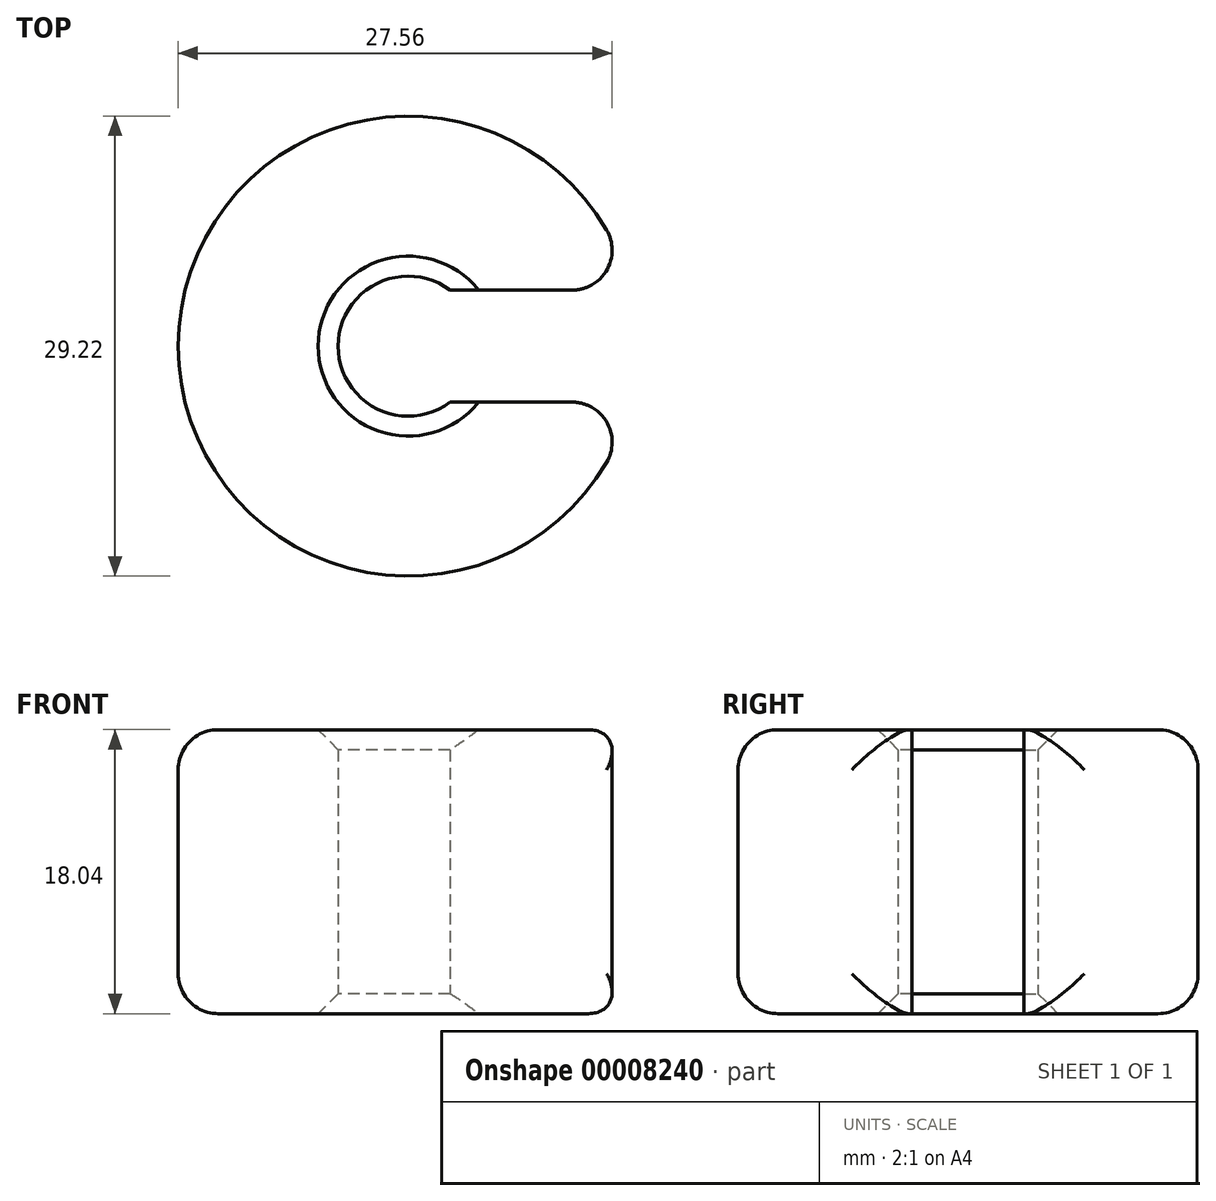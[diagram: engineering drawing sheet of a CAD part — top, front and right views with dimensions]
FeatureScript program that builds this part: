
annotation { "Feature Type Name" : "Feature", "Feature Type Description" : "" }
export const myFeature = defineFeature(function(context is Context, id is Id, definition is map)
    precondition{}
    {
        {
            var Q0;
            Q0=qCreatedBy(makeId("Top.planeOp"),FACE);
            var sketch = newSketch(context, id + "F0", { "sketchPlane" : qUnion([Q0])});
            skCircle(sketch, "E0", {"center": v(0, 0) * mm, "radius": 14.6 * mm});
            skCircle(sketch, "E1", {"center": v(0, 0) * mm, "radius": 4.45 * mm});
            skSolve(sketch);
        }
        {
            var Q0;
            Q0 = qSketchRegion(id + "F0", true);
            extrude(context, id + "F1", {"entities" : qUnion([Q0]), "endBound" : BoundingType.SYMMETRIC, "depth" : 18.03 * mm});
        }
        {
            var Q0;
            Q0=qCreatedBy(makeId("Top.planeOp"),FACE);
            var sketch = newSketch(context, id + "F2", { "sketchPlane" : qUnion([Q0])});
            skLineSegment(sketch, "E2.bottom", {"start": v(23.98, -3.56) * mm, "end": v(0, -3.56) * mm});
            skLineSegment(sketch, "E2.top", {"start": v(23.98, 3.56) * mm, "end": v(0, 3.56) * mm});
            skLineSegment(sketch, "E2.left", {"start": v(23.98, -3.56) * mm, "end": v(23.98, 3.56) * mm});
            skLineSegment(sketch, "E2.right", {"start": v(0, -3.56) * mm, "end": v(0, 3.56) * mm});
            skSolve(sketch);
        }
        {
            var Q0;
            Q0 = qSketchRegion(id + "F2", true);
            var Q1;
            Q1=makeQuery(id+"F1.opExtrude","CAP_FACE",FACE,{"disambiguationData":[OSD([sQuery(id+"F0.wireOp",EDGE,"E0"),sQuery(id+"F0.wireOp",EDGE,"E1")])],"isStart":true});
            extrude(context, id + "F3", {"entities" : qUnion([Q0]), "operationType" : NewBodyOperationType.REMOVE, "endBound" : BoundingType.UP_TO_SURFACE, "oppositeDirection" : true, "endBoundEntityFace" : qUnion([Q1]), "depth" : 25.4 * mm, "hasSecondDirection" : true, "secondDirectionOppositeDirection" : false, "secondDirectionDepth" : 25.4 * mm});
        }
        {
            var Q0;
            Q0=makeQuery(id+"F3.boolean.opBoolean","INTERSECT",EDGE,{"derivedFrom":[makeQuery(id+"F1.opExtrude","SWEPT_FACE",FACE,{"disambiguationData":[OSD([sQuery(id+"F0.wireOp",EDGE,"E0")])]}),makeQuery(id+"F3.opExtrude","SWEPT_FACE",FACE,{"disambiguationData":[OSD([sQuery(id+"F2.wireOp",EDGE,"E2.top")])]})]});
            var Q1;
            Q1=makeQuery(id+"F3.boolean.opBoolean","INTERSECT",EDGE,{"derivedFrom":[makeQuery(id+"F1.opExtrude","SWEPT_FACE",FACE,{"disambiguationData":[OSD([sQuery(id+"F0.wireOp",EDGE,"E0")])]}),makeQuery(id+"F3.opExtrude","SWEPT_FACE",FACE,{"disambiguationData":[OSD([sQuery(id+"F2.wireOp",EDGE,"E2.bottom")])]})]});
            fillet(context, id + "F4", {"entities" : qUnion([Q0, Q1]), "radius" : 2.54 * mm, "tangentPropagation" : true, "allowEdgeOverflow" : false});
        }
        {
            var Q0;
            Q0=makeQuery(id+"F1.opExtrude","SWEPT_FACE",FACE,{"disambiguationData":[OSD([sQuery(id+"F0.wireOp",EDGE,"E0")])]});
            var Q1;
            Q1=makeQuery(id+"F1.opExtrude","CAP_EDGE",EDGE,{"disambiguationData":[OSD([sQuery(id+"F0.wireOp",EDGE,"E0")])],"isStart":false});
            fillet(context, id + "F5", {"entities" : qUnion([Q0, Q1]), "radius" : 2.54 * mm, "allowEdgeOverflow" : false});
        }
        {
            var Q0;
            Q0=makeQuery(id+"F1.opExtrude","CAP_EDGE",EDGE,{"disambiguationData":[OSD([sQuery(id+"F0.wireOp",EDGE,"E1")])],"isStart":false});
            var Q1;
            Q1=makeQuery(id+"F1.opExtrude","CAP_EDGE",EDGE,{"disambiguationData":[OSD([sQuery(id+"F0.wireOp",EDGE,"E1")])],"isStart":true});
            chamfer(context, id + "F6", {"entities" : qUnion([Q0, Q1]), "width" : 1.27 * mm, "tangentPropagation" : true});
        }
    });
